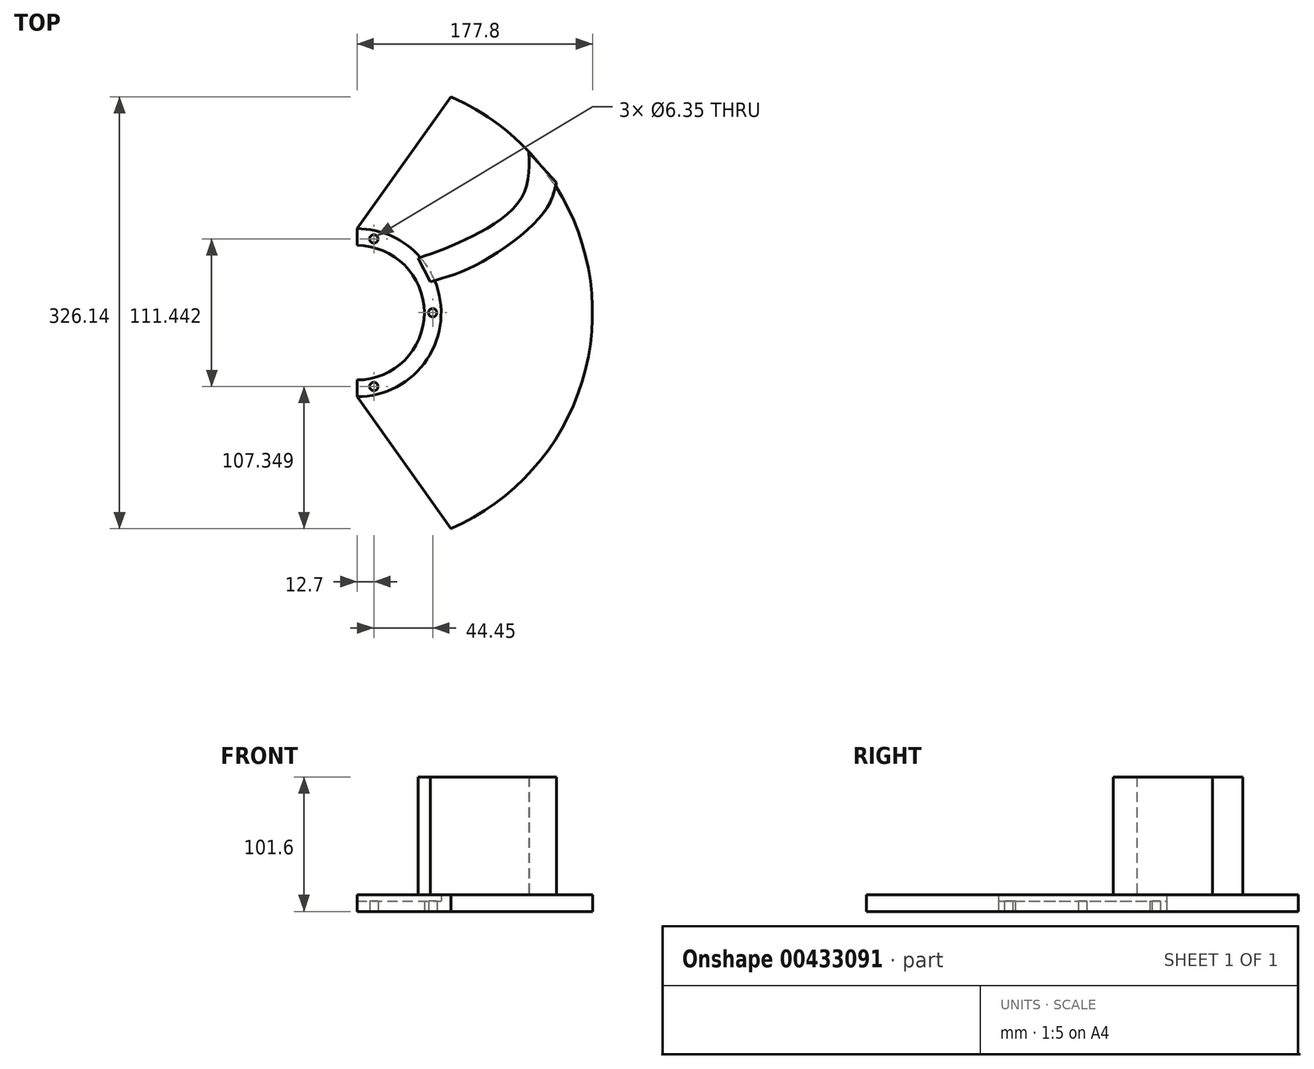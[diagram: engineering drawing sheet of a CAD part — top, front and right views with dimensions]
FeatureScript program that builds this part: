
annotation { "Feature Type Name" : "Feature", "Feature Type Description" : "" }
export const myFeature = defineFeature(function(context is Context, id is Id, definition is map)
    precondition{}
    {
        {
            var Q0;
            Q0=qCreatedBy(makeId("Top.planeOp"),FACE);
            var sketch = newSketch(context, id + "F0", { "sketchPlane" : qUnion([Q0])});
            skArc(sketch, "E0", {"start": v(0, -50.8) * mm, "mid": v(50.8, 0) * mm, "end": v(0, 50.8) * mm});
            skArc(sketch, "E1", {"start": v(0, -63.5) * mm, "mid": v(63.5, 0) * mm, "end": v(0, 63.5) * mm});
            skLineSegment(sketch, "E2", {"start": v(0, 50.8) * mm, "end": v(0, 63.5) * mm});
            skLineSegment(sketch, "E3", {"start": v(0, -50.8) * mm, "end": v(0, -63.5) * mm});
            skCircle(sketch, "E4", {"center": v(12.7, 55.72) * mm, "radius": 3.18 * mm});
            skCircle(sketch, "E5", {"center": v(57.15, 0) * mm, "radius": 3.18 * mm});
            skCircle(sketch, "E6", {"center": v(0, 0) * mm, "radius": 57.15 * mm, "construction": true});
            skCircle(sketch, "E7.MirrorC", {"center": v(12.7, -55.72) * mm, "radius": 3.18 * mm});
            skSolve(sketch);
        }
        {
            var Q0;
            Q0 = qSketchRegion(id + "F0", true);
            extrude(context, id + "F1", {"entities" : qUnion([Q0]), "depth" : 7.94 * mm});
        }
        {
            var Q0;
            Q0=qCreatedBy(makeId("Top.planeOp"),FACE);
            var sketch = newSketch(context, id + "F2", { "sketchPlane" : qUnion([Q0])});
            skArc(sketch, "E8", {"start": v(0, -63.5) * mm, "mid": v(63.5, 0) * mm, "end": v(0, 63.5) * mm});
            skArc(sketch, "E9", {"start": v(70.85, -163.07) * mm, "mid": v(177.8, 0) * mm, "end": v(70.85, 163.07) * mm});
            skLineSegment(sketch, "E10", {"start": v(-153.6, 0) * mm, "end": v(89.83, 176.87) * mm, "construction": true});
            skLineSegment(sketch, "E11.MirrorCS", {"start": v(-153.6, 0) * mm, "end": v(89.83, -176.87) * mm, "construction": true});
            skLineSegment(sketch, "E12", {"start": v(0, 63.5) * mm, "end": v(70.85, 163.07) * mm});
            skLineSegment(sketch, "E13", {"start": v(0, -63.5) * mm, "end": v(70.85, -163.07) * mm});
            skSolve(sketch);
        }
        {
            var Q0;
            Q0 = qSketchRegion(id + "F2", true);
            extrude(context, id + "F3", {"entities" : qUnion([Q0]), "operationType" : NewBodyOperationType.ADD, "depth" : 12.7 * mm});
        }
        {
            var Q0;
            Q0=qCreatedBy(makeId("Top.planeOp"),FACE);
            cPlane(context, id + "F4", {"entities" : qUnion([Q0]), "cplaneType" : CPlaneType.OFFSET, "offset" : 12.7 * mm, "width" : 152.4 * mm, "height" : 152.4 * mm});
        }
        {
            var Q0;
            Q0=qCreatedBy(id+"F4.planeOp",FACE);
            var sketch = newSketch(context, id + "F5", { "sketchPlane" : qUnion([Q0])});
            skFitSpline(sketch, "E14", {"points": [v(46.19, 41.18) * mm, v(86.38, 57.34) * mm, v(124.21, 86.9) * mm, v(129.73, 121.18) * mm], "startDerivative": vector(115.58, 40.57) * mm, "endDerivative": vector(-2.71, 118.1) * mm});
            skFitSpline(sketch, "E15", {"points": [v(55.25, 23.45) * mm, v(92.3, 37.24) * mm, v(140.77, 75.47) * mm, v(150.62, 98.32) * mm], "startDerivative": vector(105.48, 29.16) * mm, "endDerivative": vector(20.44, 83.5) * mm});
            skLineSegment(sketch, "E16", {"start": v(129.73, 121.18) * mm, "end": v(150.62, 98.32) * mm});
            skLineSegment(sketch, "E17", {"start": v(46.19, 41.18) * mm, "end": v(55.25, 23.45) * mm});
            skSolve(sketch);
        }
        {
            var Q0;
            Q0 = qSketchRegion(id + "F5", true);
            extrude(context, id + "F6", {"entities" : qUnion([Q0]), "operationType" : NewBodyOperationType.ADD, "depth" : 88.9 * mm});
        }
    });
